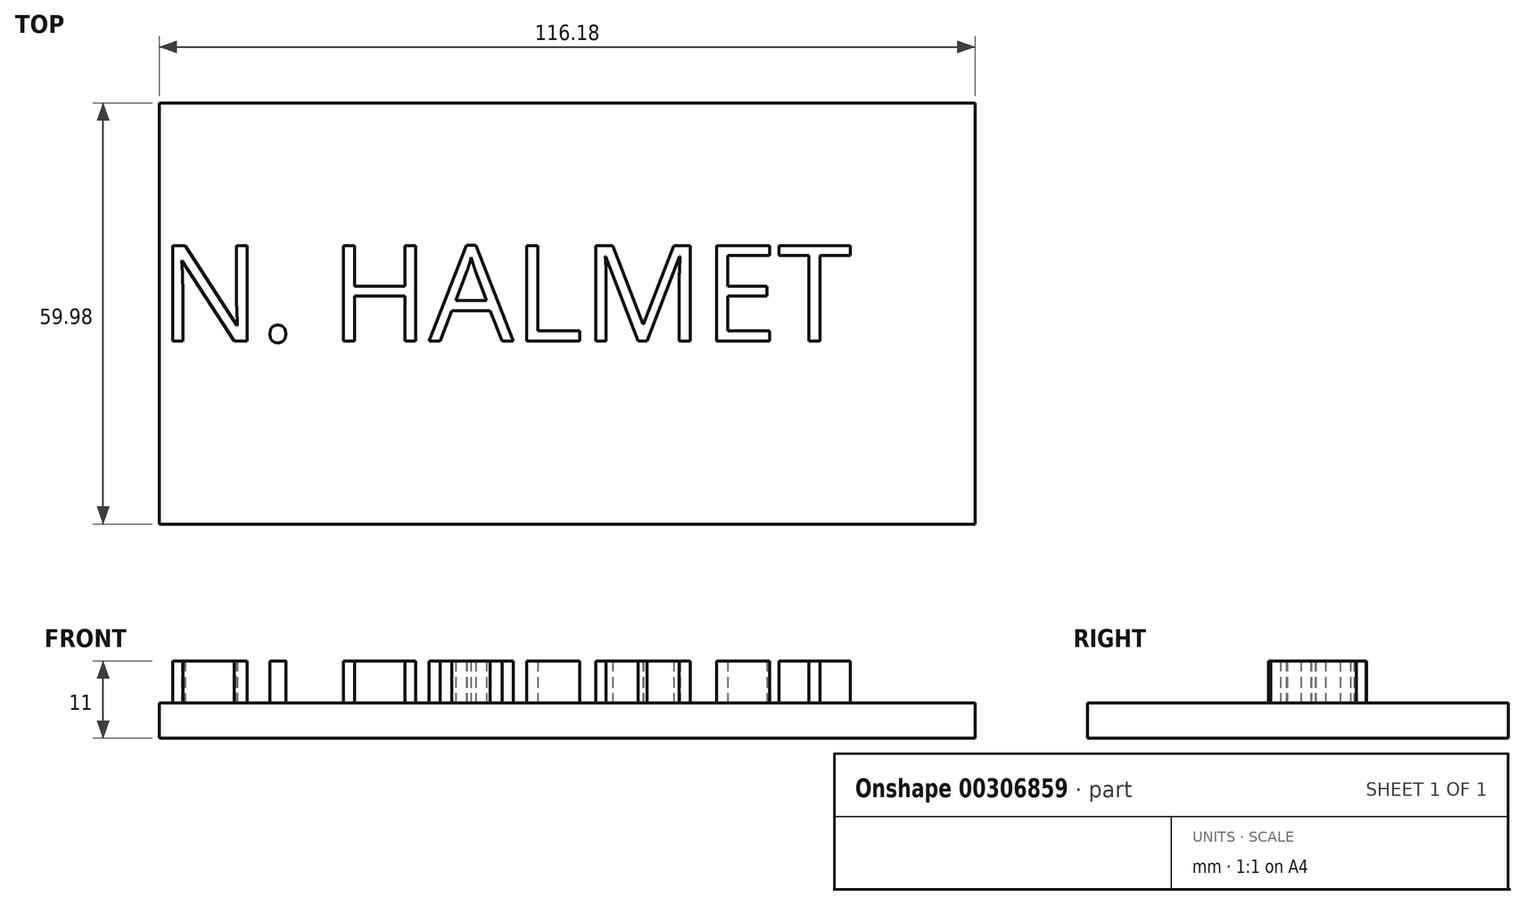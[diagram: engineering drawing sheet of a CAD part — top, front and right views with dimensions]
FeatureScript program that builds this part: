
annotation { "Feature Type Name" : "Feature", "Feature Type Description" : "" }
export const myFeature = defineFeature(function(context is Context, id is Id, definition is map)
    precondition{}
    {
        {
            var Q0;
            Q0=qCreatedBy(makeId("Top.planeOp"),FACE);
            var sketch = newSketch(context, id + "F0", { "sketchPlane" : qUnion([Q0])});
            skLineSegment(sketch, "E0.bottom", {"start": v(-116.18, -8.9) * mm, "end": v(0, -8.9) * mm});
            skLineSegment(sketch, "E0.top", {"start": v(-116.18, 51.08) * mm, "end": v(0, 51.08) * mm});
            skLineSegment(sketch, "E0.left", {"start": v(-116.18, -8.9) * mm, "end": v(-116.18, 51.08) * mm});
            skLineSegment(sketch, "E0.right", {"start": v(0, -8.9) * mm, "end": v(0, 51.08) * mm});
            skSolve(sketch);
        }
        {
            var Q0;
            Q0=makeQuery(id+"F0.imprint","IMPRINT",FACE,{"disambiguationData":[TD([[makeQuery(id+"F0.imprint","IMPRINT",EDGE,{"derivedFrom":sQuery(id+"F0.wireOp",EDGE,"E0.bottom")}),1.0]])]});
            extrude(context, id + "F1", {"entities" : qUnion([Q0]), "depth" : 5 * mm});
        }
        {
            var Q0;
            Q0=makeQuery(id+"F1.opExtrude","CAP_FACE",FACE,{"disambiguationData":[OSD([sQuery(id+"F0.wireOp",EDGE,"E0.bottom"),sQuery(id+"F0.wireOp",EDGE,"E0.top"),sQuery(id+"F0.wireOp",EDGE,"E0.left"),sQuery(id+"F0.wireOp",EDGE,"E0.right")])],"isStart":false});
            var sketch = newSketch(context, id + "F2", { "sketchPlane" : qUnion([Q0])});
            skText(sketch, "E1", { "text": "N. HALMET", "fontName": "OpenSans-Regular.ttf"});
            const initialGuessF2  = {"E1": [-0.11618, 0.0172, 1, 0, 0.0137]};
            skSetInitialGuess(sketch, initialGuessF2);
            skSolve(sketch);
        }
        {
            var Q0;
            Q0=qSketchRegion(id+"F2",true);
            extrude(context, id + "F3", {"entities" : qUnion([Q0]), "operationType" : NewBodyOperationType.ADD, "depth" : 6 * mm});
        }
    });
